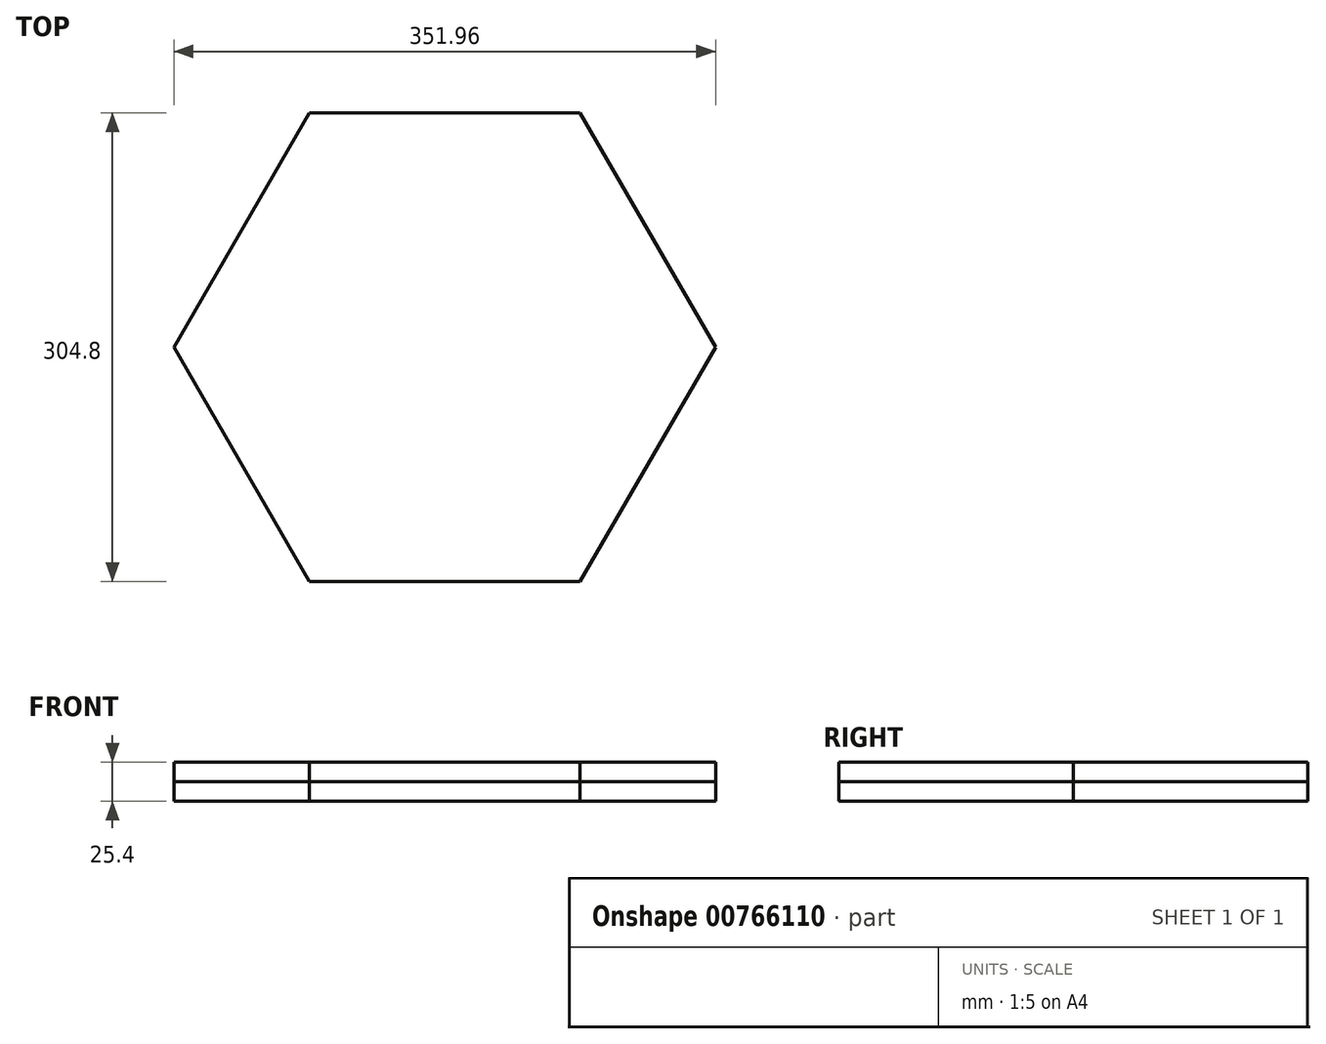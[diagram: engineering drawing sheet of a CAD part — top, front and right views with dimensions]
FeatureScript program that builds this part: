
annotation { "Feature Type Name" : "Feature", "Feature Type Description" : "" }
export const myFeature = defineFeature(function(context is Context, id is Id, definition is map)
    precondition{}
    {
        {
            var Q0;
            Q0=qCreatedBy(makeId("Top.planeOp"),FACE);
            var sketch = newSketch(context, id + "F0", { "sketchPlane" : qUnion([Q0])});
            skCircle(sketch, "E0", {"center": v(0, 0) * mm, "radius": 152.4 * mm});
            skLineSegment(sketch, "E1", {"start": v(0, 0) * mm, "end": v(107.42, 62.02) * mm, "construction": true});
            skLineSegment(sketch, "E2.MirrorCS", {"start": v(0, 0) * mm, "end": v(-107.42, 62.02) * mm, "construction": true});
            skLineSegment(sketch, "E3.MirrorCS", {"start": v(0, 0) * mm, "end": v(107.42, -62.02) * mm, "construction": true});
            skLineSegment(sketch, "E4.MirrorCS", {"start": v(0, 0) * mm, "end": v(-107.42, -62.02) * mm, "construction": true});
            skLineSegment(sketch, "E5", {"start": v(0, 0) * mm, "end": v(0, -111.89) * mm, "construction": true});
            skLineSegment(sketch, "E6", {"start": v(0, -152.4) * mm, "end": v(54.59, -152.4) * mm, "construction": true});
            skLineSegment(sketch, "E7", {"start": v(131.98, -76.2) * mm, "end": v(175.98, 0) * mm, "construction": true});
            skLineSegment(sketch, "E8", {"start": v(131.98, 76.2) * mm, "end": v(98.61, 134) * mm, "construction": true});
            skLineSegment(sketch, "E9.MirrorCS", {"start": v(0, 0) * mm, "end": v(0, 111.89) * mm, "construction": true});
            skLineSegment(sketch, "E10", {"start": v(0, 152.4) * mm, "end": v(-86.75, 152.4) * mm, "construction": true});
            skLineSegment(sketch, "E11", {"start": v(-131.98, 76.2) * mm, "end": v(-172.27, 6.42) * mm, "construction": true});
            skLineSegment(sketch, "E12", {"start": v(-131.98, -76.2) * mm, "end": v(-91.44, -146.43) * mm, "construction": true});
            skLineSegment(sketch, "E13.MirrorCS", {"start": v(-131.98, 76.2) * mm, "end": v(-91.7, 145.98) * mm, "construction": true});
            skLineSegment(sketch, "E14.MirrorCS", {"start": v(131.98, -76.2) * mm, "end": v(87.99, -152.4) * mm, "construction": true});
            skLineSegment(sketch, "E15.MirrorCS", {"start": v(131.98, 76.2) * mm, "end": v(165.35, 18.4) * mm, "construction": true});
            skLineSegment(sketch, "E16.MirrorCS", {"start": v(0, 152.4) * mm, "end": v(86.75, 152.4) * mm, "construction": true});
            skLineSegment(sketch, "E17.MirrorCS", {"start": v(0, -152.4) * mm, "end": v(-54.59, -152.4) * mm, "construction": true});
            skLineSegment(sketch, "E18.MirrorCS", {"start": v(-131.98, -76.2) * mm, "end": v(-172.53, -5.97) * mm, "construction": true});
            skLineSegment(sketch, "E19", {"start": v(-131.98, -76.2) * mm, "end": v(-87.99, -152.4) * mm});
            skLineSegment(sketch, "E20", {"start": v(-87.99, -152.4) * mm, "end": v(87.99, -152.4) * mm});
            skLineSegment(sketch, "E21", {"start": v(87.99, -152.4) * mm, "end": v(175.98, 0) * mm});
            skLineSegment(sketch, "E22", {"start": v(175.98, 0) * mm, "end": v(87.99, 152.4) * mm});
            skLineSegment(sketch, "E23", {"start": v(87.99, 152.4) * mm, "end": v(-87.99, 152.4) * mm});
            skLineSegment(sketch, "E24", {"start": v(-87.99, 152.4) * mm, "end": v(-175.98, 0) * mm});
            skLineSegment(sketch, "E25", {"start": v(-175.98, 0) * mm, "end": v(-131.98, -76.2) * mm});
            skLineSegment(sketch, "E26", {"start": v(-131.98, 76.2) * mm, "end": v(42.5, 973.8) * mm, "construction": true});
            skLineSegment(sketch, "E27", {"start": v(131.98, 76.2) * mm, "end": v(822.09, -523.7) * mm, "construction": true});
            skLineSegment(sketch, "E28", {"start": v(131.98, -76.2) * mm, "end": v(-42.5, -973.8) * mm, "construction": true});
            skLineSegment(sketch, "E29", {"start": v(0, -152.4) * mm, "end": v(-864.58, -450.1) * mm, "construction": true});
            skLineSegment(sketch, "E30", {"start": v(-131.98, -76.2) * mm, "end": v(-822.09, 523.7) * mm, "construction": true});
            skLineSegment(sketch, "E31.MirrorCS", {"start": v(131.98, -76.2) * mm, "end": v(822.09, 523.7) * mm, "construction": true});
            skLineSegment(sketch, "E32", {"start": v(131.98, 76.2) * mm, "end": v(-42.5, 973.8) * mm, "construction": true});
            skLineSegment(sketch, "E33", {"start": v(0, 152.4) * mm, "end": v(864.58, 450.1) * mm, "construction": true});
            skLineSegment(sketch, "E34", {"start": v(0, 152.4) * mm, "end": v(-864.58, 450.1) * mm, "construction": true});
            skLineSegment(sketch, "E35", {"start": v(-131.98, 76.2) * mm, "end": v(-822.09, -523.7) * mm, "construction": true});
            skLineSegment(sketch, "E36", {"start": v(-131.98, -76.2) * mm, "end": v(42.5, -973.8) * mm, "construction": true});
            skLineSegment(sketch, "E37", {"start": v(0, -152.4) * mm, "end": v(864.58, -450.1) * mm, "construction": true});
            skLineSegment(sketch, "E38", {"start": v(-131.98, 76.2) * mm, "end": v(-822.09, -523.7) * mm});
            skLineSegment(sketch, "E39", {"start": v(-131.98, -76.2) * mm, "end": v(-822.09, 523.7) * mm});
            skLineSegment(sketch, "E40", {"start": v(-131.98, -76.2) * mm, "end": v(42.5, -973.8) * mm});
            skLineSegment(sketch, "E41", {"start": v(0, -152.4) * mm, "end": v(-864.58, -450.1) * mm});
            skLineSegment(sketch, "E42", {"start": v(0, -152.4) * mm, "end": v(864.58, -450.1) * mm});
            skLineSegment(sketch, "E43", {"start": v(131.98, -76.2) * mm, "end": v(-42.5, -973.8) * mm});
            skLineSegment(sketch, "E44", {"start": v(131.98, -76.2) * mm, "end": v(822.09, 523.7) * mm});
            skLineSegment(sketch, "E45", {"start": v(131.98, 76.2) * mm, "end": v(822.09, -523.7) * mm});
            skLineSegment(sketch, "E46", {"start": v(131.98, 76.2) * mm, "end": v(-42.5, 973.8) * mm});
            skLineSegment(sketch, "E47", {"start": v(0, 152.4) * mm, "end": v(864.58, 450.1) * mm});
            skLineSegment(sketch, "E48", {"start": v(0, 152.4) * mm, "end": v(-864.58, 450.1) * mm});
            skLineSegment(sketch, "E49", {"start": v(-131.98, 76.2) * mm, "end": v(42.5, 973.8) * mm});
            skLineSegment(sketch, "E50", {"start": v(42.5, 973.8) * mm, "end": v(-822.09, -523.7) * mm});
            skLineSegment(sketch, "E51", {"start": v(-822.09, 523.7) * mm, "end": v(42.5, -973.8) * mm});
            skLineSegment(sketch, "E52", {"start": v(-864.58, -450.1) * mm, "end": v(864.58, -450.1) * mm});
            skLineSegment(sketch, "E53", {"start": v(-42.5, -973.8) * mm, "end": v(822.09, 523.7) * mm});
            skLineSegment(sketch, "E54", {"start": v(-864.58, 450.1) * mm, "end": v(864.58, 450.1) * mm});
            skLineSegment(sketch, "E55", {"start": v(822.09, -523.7) * mm, "end": v(-42.5, 973.8) * mm});
            skLineSegment(sketch, "E56", {"start": v(87.99, 152.4) * mm, "end": v(259.87, 450.1) * mm});
            skLineSegment(sketch, "E57", {"start": v(-86.75, 152.4) * mm, "end": v(-259.87, 450.1) * mm});
            skLineSegment(sketch, "E58", {"start": v(-259.87, 450.1) * mm, "end": v(259.87, 450.1) * mm});
            skLineSegment(sketch, "E59", {"start": v(-175.98, 0) * mm, "end": v(-519.73, 0) * mm});
            skLineSegment(sketch, "E60", {"start": v(-519.73, 0) * mm, "end": v(-259.87, 450.1) * mm});
            skLineSegment(sketch, "E61", {"start": v(-87.99, -152.4) * mm, "end": v(-259.87, -450.1) * mm});
            skLineSegment(sketch, "E62", {"start": v(-259.87, -450.1) * mm, "end": v(-519.73, 0) * mm});
            skLineSegment(sketch, "E63", {"start": v(87.99, -152.4) * mm, "end": v(259.87, -450.1) * mm});
            skLineSegment(sketch, "E64", {"start": v(259.87, -450.1) * mm, "end": v(-259.87, -450.1) * mm});
            skLineSegment(sketch, "E65", {"start": v(175.98, 0) * mm, "end": v(519.73, 0) * mm});
            skLineSegment(sketch, "E66", {"start": v(519.73, 0) * mm, "end": v(259.87, -450.1) * mm});
            skSolve(sketch);
        }
        {
            var Q0;
            {var subQ0=sQuery(id+"F0.wireOp",EDGE,"E0");var subQ4=makeQuery(id+"F0.imprint","INTERSECT",VERTEX,{"derivedFrom":[subQ0,sQuery(id+"F0.wireOp",EDGE,"E23")]});Q0=makeQuery(id+"F0.imprint","IMPRINT",FACE,{"disambiguationData":[TD([[makeQuery(id+"F0.imprint","IMPRINT",EDGE,{"disambiguationData":[TD([[subQ4,1.0]])],"derivedFrom":subQ0}),1.0]])]});}
            var Q1;
            {var subQ0=sQuery(id+"F0.wireOp",EDGE,"E19");Q1=makeQuery(id+"F0.imprint","IMPRINT",FACE,{"disambiguationData":[TD([[makeQuery(id+"F0.imprint","IMPRINT",EDGE,{"derivedFrom":subQ0}),1.0]])]});}
            var Q2;
            {var subQ0=sQuery(id+"F0.wireOp",EDGE,"E25");Q2=makeQuery(id+"F0.imprint","IMPRINT",FACE,{"disambiguationData":[TD([[makeQuery(id+"F0.imprint","IMPRINT",EDGE,{"derivedFrom":subQ0}),1.0]])]});}
            var Q3;
            {var subQ0=sQuery(id+"F0.wireOp",EDGE,"E23");var subQ1=sQuery(id+"F0.wireOp",EDGE,"E0");var subQ2=makeQuery(id+"F0.imprint","INTERSECT",VERTEX,{"derivedFrom":[subQ1,subQ0]});Q3=makeQuery(id+"F0.imprint","IMPRINT",FACE,{"disambiguationData":[TD([[makeQuery(id+"F0.imprint","IMPRINT",EDGE,{"disambiguationData":[TD([[subQ2,-1.0]])],"derivedFrom":subQ1}),-1.0]])]});}
            var Q4;
            {var subQ0=sQuery(id+"F0.wireOp",EDGE,"E23");var subQ1=sQuery(id+"F0.wireOp",EDGE,"E0");var subQ2=makeQuery(id+"F0.imprint","INTERSECT",VERTEX,{"derivedFrom":[subQ1,subQ0]});Q4=makeQuery(id+"F0.imprint","IMPRINT",FACE,{"disambiguationData":[TD([[makeQuery(id+"F0.imprint","IMPRINT",EDGE,{"disambiguationData":[TD([[subQ2,1.0]])],"derivedFrom":subQ1}),-1.0]])]});}
            var Q5;
            {var subQ0=sQuery(id+"F0.wireOp",EDGE,"E22");var subQ1=sQuery(id+"F0.wireOp",EDGE,"E0");var subQ2=makeQuery(id+"F0.imprint","INTERSECT",VERTEX,{"derivedFrom":[subQ1,subQ0]});Q5=makeQuery(id+"F0.imprint","IMPRINT",FACE,{"disambiguationData":[TD([[makeQuery(id+"F0.imprint","IMPRINT",EDGE,{"disambiguationData":[TD([[subQ2,1.0]])],"derivedFrom":subQ1}),-1.0]])]});}
            var Q6;
            {var subQ0=sQuery(id+"F0.wireOp",EDGE,"E20");var subQ1=sQuery(id+"F0.wireOp",EDGE,"E0");var subQ2=makeQuery(id+"F0.imprint","INTERSECT",VERTEX,{"derivedFrom":[subQ1,subQ0]});Q6=makeQuery(id+"F0.imprint","IMPRINT",FACE,{"disambiguationData":[TD([[makeQuery(id+"F0.imprint","IMPRINT",EDGE,{"disambiguationData":[TD([[subQ2,-1.0]])],"derivedFrom":subQ1}),-1.0]])]});}
            extrude(context, id + "F1", {"entities" : qUnion([Q0, Q1, Q2, Q3, Q4, Q5, Q6]), "depth" : 12.7 * mm, "offsetDistance" : 25.4 * mm});
        }
        {
            var Q0;
            {var subQ0=sQuery(id+"F0.wireOp",EDGE,"E0");var subQ4=makeQuery(id+"F0.imprint","INTERSECT",VERTEX,{"derivedFrom":[subQ0,sQuery(id+"F0.wireOp",EDGE,"E23")]});Q0=makeQuery(id+"F0.imprint","IMPRINT",FACE,{"disambiguationData":[TD([[makeQuery(id+"F0.imprint","IMPRINT",EDGE,{"disambiguationData":[TD([[subQ4,1.0]])],"derivedFrom":subQ0}),1.0]])]});}
            var Q1;
            {var subQ0=sQuery(id+"F0.wireOp",EDGE,"E25");Q1=makeQuery(id+"F0.imprint","IMPRINT",FACE,{"disambiguationData":[TD([[makeQuery(id+"F0.imprint","IMPRINT",EDGE,{"derivedFrom":subQ0}),1.0]])]});}
            var Q2;
            {var subQ0=sQuery(id+"F0.wireOp",EDGE,"E23");var subQ1=sQuery(id+"F0.wireOp",EDGE,"E0");var subQ2=makeQuery(id+"F0.imprint","INTERSECT",VERTEX,{"derivedFrom":[subQ1,subQ0]});Q2=makeQuery(id+"F0.imprint","IMPRINT",FACE,{"disambiguationData":[TD([[makeQuery(id+"F0.imprint","IMPRINT",EDGE,{"disambiguationData":[TD([[subQ2,-1.0]])],"derivedFrom":subQ1}),-1.0]])]});}
            var Q3;
            {var subQ0=sQuery(id+"F0.wireOp",EDGE,"E23");var subQ1=sQuery(id+"F0.wireOp",EDGE,"E0");var subQ2=makeQuery(id+"F0.imprint","INTERSECT",VERTEX,{"derivedFrom":[subQ1,subQ0]});Q3=makeQuery(id+"F0.imprint","IMPRINT",FACE,{"disambiguationData":[TD([[makeQuery(id+"F0.imprint","IMPRINT",EDGE,{"disambiguationData":[TD([[subQ2,1.0]])],"derivedFrom":subQ1}),-1.0]])]});}
            var Q4;
            {var subQ0=sQuery(id+"F0.wireOp",EDGE,"E22");var subQ1=sQuery(id+"F0.wireOp",EDGE,"E0");var subQ2=makeQuery(id+"F0.imprint","INTERSECT",VERTEX,{"derivedFrom":[subQ1,subQ0]});Q4=makeQuery(id+"F0.imprint","IMPRINT",FACE,{"disambiguationData":[TD([[makeQuery(id+"F0.imprint","IMPRINT",EDGE,{"disambiguationData":[TD([[subQ2,1.0]])],"derivedFrom":subQ1}),-1.0]])]});}
            var Q5;
            {var subQ0=sQuery(id+"F0.wireOp",EDGE,"E20");var subQ1=sQuery(id+"F0.wireOp",EDGE,"E0");var subQ2=makeQuery(id+"F0.imprint","INTERSECT",VERTEX,{"derivedFrom":[subQ1,subQ0]});Q5=makeQuery(id+"F0.imprint","IMPRINT",FACE,{"disambiguationData":[TD([[makeQuery(id+"F0.imprint","IMPRINT",EDGE,{"disambiguationData":[TD([[subQ2,-1.0]])],"derivedFrom":subQ1}),-1.0]])]});}
            var Q6;
            {var subQ0=sQuery(id+"F0.wireOp",EDGE,"E19");Q6=makeQuery(id+"F0.imprint","IMPRINT",FACE,{"disambiguationData":[TD([[makeQuery(id+"F0.imprint","IMPRINT",EDGE,{"derivedFrom":subQ0}),1.0]])]});}
            extrude(context, id + "F2", {"entities" : qUnion([Q0, Q1, Q2, Q3, Q4, Q5, Q6]), "oppositeDirection" : true, "depth" : 12.7 * mm, "offsetDistance" : 25.4 * mm});
        }
    });
